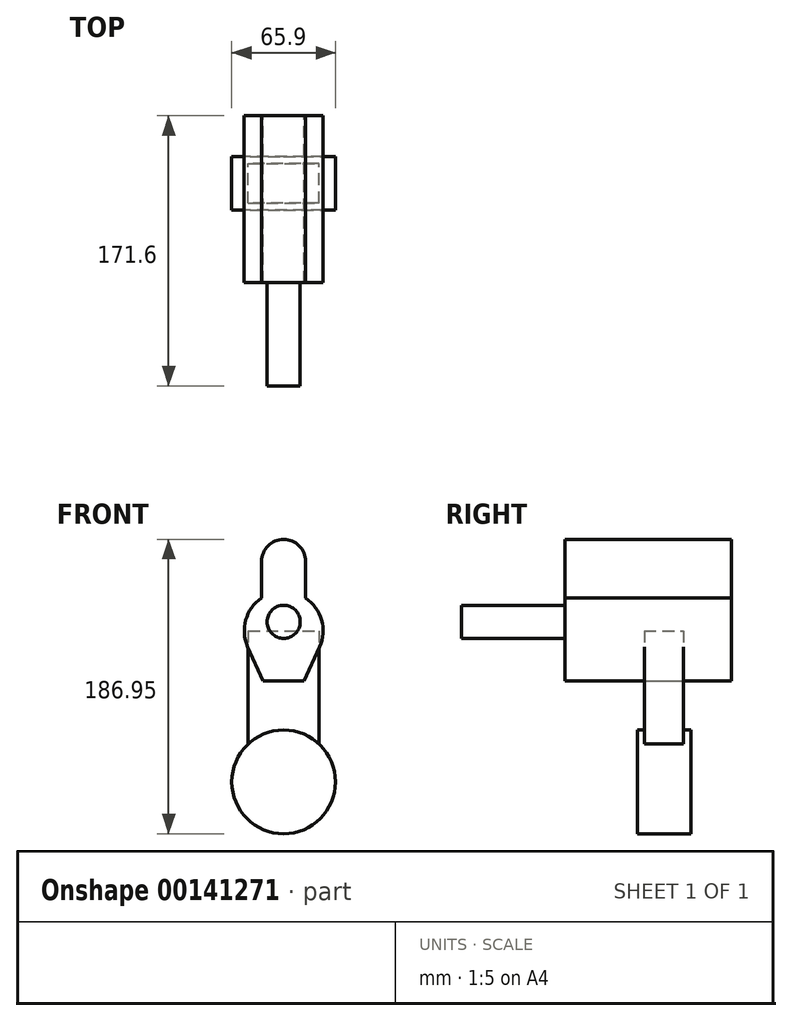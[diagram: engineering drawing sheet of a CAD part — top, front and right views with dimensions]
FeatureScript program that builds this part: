
annotation { "Feature Type Name" : "Feature", "Feature Type Description" : "" }
export const myFeature = defineFeature(function(context is Context, id is Id, definition is map)
    precondition{}
    {
        {
            var Q0;
            Q0=qCreatedBy(makeId("Front.planeOp"),FACE);
            var sketch = newSketch(context, id + "F0", { "sketchPlane" : qUnion([Q0])});
            skCircle(sketch, "E0", {"center": v(0, 0) * mm, "radius": 32.95 * mm});
            skCircle(sketch, "E1", {"center": v(0, 0) * mm, "radius": 20.6 * mm});
            skLineSegment(sketch, "E2.bottom", {"start": v(-22.5, 96) * mm, "end": v(22.5, 96) * mm});
            skLineSegment(sketch, "E2.left", {"start": v(-22.5, 96) * mm, "end": v(-22.5, 24.07) * mm});
            skLineSegment(sketch, "E2.right", {"start": v(22.5, 96) * mm, "end": v(22.5, 24.07) * mm});
            skArc(sketch, "E3", {"start": v(22.8, 85.73) * mm, "mid": v(24.05, 102.82) * mm, "end": v(14, 116.71) * mm});
            skLineSegment(sketch, "E4", {"start": v(-13, 64) * mm, "end": v(13, 64) * mm});
            skLineSegment(sketch, "E5", {"start": v(13, 64) * mm, "end": v(22.8, 85.73) * mm});
            skLineSegment(sketch, "E6", {"start": v(-13, 64) * mm, "end": v(-22.8, 85.73) * mm});
            skLineSegment(sketch, "E7", {"start": v(-14, 116.71) * mm, "end": v(-14, 140) * mm});
            skLineSegment(sketch, "E8", {"start": v(14, 116.71) * mm, "end": v(14, 140) * mm});
            skArc(sketch, "E9", {"start": v(14, 140) * mm, "mid": v(0, 154) * mm, "end": v(-14, 140) * mm});
            skArc(sketch, "E10.trimOffspring", {"start": v(-14, 116.71) * mm, "mid": v(-24.05, 102.82) * mm, "end": v(-22.8, 85.73) * mm});
            skSolve(sketch);
        }
        {
            var Q0;
            {var subQ5=sQuery(id+"F0.wireOp",EDGE,"E2.left");var subQ8=sQuery(id+"F0.wireOp",EDGE,"E0");var subQ9=makeQuery(id+"F0.imprint","INTERSECT",VERTEX,{"derivedFrom":[subQ8,subQ5]});Q0=makeQuery(id+"F0.imprint","IMPRINT",FACE,{"disambiguationData":[TD([[makeQuery(id+"F0.imprint","IMPRINT",EDGE,{"disambiguationData":[TD([[subQ9,-1.0]])],"derivedFrom":subQ8}),1.0]])]});}
            var Q1;
            {var subQ0=sQuery(id+"F0.wireOp",EDGE,"E2.top");var subQ1=sQuery(id+"F0.wireOp",EDGE,"E1");var subQ2=makeQuery(id+"F0.imprint","INTERSECT",VERTEX,{"disambiguationData":[OD(0.0)],"derivedFrom":[subQ1,subQ0]});Q1=makeQuery(id+"F0.imprint","IMPRINT",FACE,{"disambiguationData":[TD([[makeQuery(id+"F0.imprint","IMPRINT",EDGE,{"disambiguationData":[TD([[subQ2,1.0]])],"derivedFrom":subQ1}),1.0]])]});}
            var Q2;
            {var subQ0=sQuery(id+"F0.wireOp",EDGE,"E2.top");var subQ1=sQuery(id+"F0.wireOp",EDGE,"E1");var subQ2=makeQuery(id+"F0.imprint","INTERSECT",VERTEX,{"disambiguationData":[OD(0.0)],"derivedFrom":[subQ1,subQ0]});Q2=makeQuery(id+"F0.imprint","IMPRINT",FACE,{"disambiguationData":[TD([[makeQuery(id+"F0.imprint","IMPRINT",EDGE,{"disambiguationData":[TD([[subQ2,-1.0]])],"derivedFrom":subQ1}),1.0]])]});}
            var Q3;
            {var subQ5=sQuery(id+"F0.wireOp",EDGE,"E2.left");var subQ8=sQuery(id+"F0.wireOp",EDGE,"E0");var subQ9=makeQuery(id+"F0.imprint","INTERSECT",VERTEX,{"derivedFrom":[subQ8,subQ5]});Q3=makeQuery(id+"F0.imprint","IMPRINT",FACE,{"disambiguationData":[TD([[makeQuery(id+"F0.imprint","IMPRINT",EDGE,{"disambiguationData":[TD([[subQ9,1.0]])],"derivedFrom":subQ8}),1.0]])]});}
            extrude(context, id + "F1", {"entities" : qUnion([Q0, Q1, Q2, Q3]), "endBound" : BoundingType.SYMMETRIC, "depth" : 34 * mm});
        }
        {
            var Q0;
            {var subQ0=sQuery(id+"F0.wireOp",EDGE,"E4");Q0=makeQuery(id+"F0.imprint","IMPRINT",FACE,{"disambiguationData":[TD([[makeQuery(id+"F0.imprint","IMPRINT",EDGE,{"derivedFrom":subQ0}),-1.0]])]});}
            var Q1;
            {var subQ2=sQuery(id+"F0.wireOp",EDGE,"E2.bottom");Q1=makeQuery(id+"F0.imprint","IMPRINT",FACE,{"disambiguationData":[TD([[makeQuery(id+"F0.imprint","IMPRINT",EDGE,{"derivedFrom":subQ2}),-1.0]])]});}
            extrude(context, id + "F2", {"entities" : qUnion([Q0, Q1]), "operationType" : NewBodyOperationType.ADD, "endBound" : BoundingType.SYMMETRIC, "depth" : 25 * mm});
        }
        {
            var Q0;
            Q0=qCreatedBy(makeId("Front.planeOp"),FACE);
            var sketch = newSketch(context, id + "F3", { "sketchPlane" : qUnion([Q0])});
            skLineSegment(sketch, "E11.0.2", {"start": v(22.5, 96) * mm, "end": v(22.5, 85.08) * mm});
            skLineSegment(sketch, "E11.0.3", {"start": v(22.5, 85.08) * mm, "end": v(22.8, 85.73) * mm});
            skArc(sketch, "E11.0.4", {"start": v(22.8, 85.73) * mm, "mid": v(24.05, 102.82) * mm, "end": v(14, 116.71) * mm});
            skLineSegment(sketch, "E11.0.5", {"start": v(14, 116.71) * mm, "end": v(14, 140) * mm});
            skArc(sketch, "E11.0.6", {"start": v(14, 140) * mm, "mid": v(0, 154) * mm, "end": v(-14, 140) * mm});
            skLineSegment(sketch, "E11.0.7", {"start": v(-14, 140) * mm, "end": v(-14, 116.71) * mm});
            skArc(sketch, "E11.0.8", {"start": v(-14, 116.71) * mm, "mid": v(-24.05, 102.82) * mm, "end": v(-22.8, 85.73) * mm});
            skLineSegment(sketch, "E11.0.9", {"start": v(-22.8, 85.73) * mm, "end": v(-22.5, 85.08) * mm});
            skLineSegment(sketch, "E12.0", {"start": v(13, 64) * mm, "end": v(22.8, 85.73) * mm});
            skLineSegment(sketch, "E12.1", {"start": v(-13, 64) * mm, "end": v(13, 64) * mm});
            skLineSegment(sketch, "E12.2", {"start": v(-13, 64) * mm, "end": v(-22.8, 85.73) * mm});
            skSolve(sketch);
        }
        {
            var Q0;
            Q0 = qSketchRegion(id + "F3", true);
            extrude(context, id + "F4", {"entities" : qUnion([Q0]), "endBound" : BoundingType.SYMMETRIC, "offsetDistance" : 25 * mm, "depth" : 86 * mm});
        }
        {
            var Q0;
            Q0=makeQuery(id+"F4.opExtrude","CAP_FACE",FACE,{"disambiguationData":[OSD([sQuery(id+"F3.wireOp",EDGE,"E11.0.4"),sQuery(id+"F3.wireOp",EDGE,"E11.0.5"),sQuery(id+"F3.wireOp",EDGE,"E11.0.6"),sQuery(id+"F3.wireOp",EDGE,"E11.0.7"),sQuery(id+"F3.wireOp",EDGE,"E11.0.8"),sQuery(id+"F3.wireOp",EDGE,"E12.0"),sQuery(id+"F3.wireOp",EDGE,"E12.1"),sQuery(id+"F3.wireOp",EDGE,"E12.2")])],"isStart":false});
            extrude(context, id + "F5", {"entities" : qUnion([Q0]), "operationType" : NewBodyOperationType.ADD, "offsetDistance" : 25 * mm, "depth" : 20 * mm});
        }
        {
            var Q0;
            Q0=makeQuery(id+"F5.opExtrude","CAP_FACE",FACE,{"disambiguationData":[OSD([sQuery(id+"F3.wireOp",EDGE,"E11.0.4"),sQuery(id+"F3.wireOp",EDGE,"E11.0.5"),sQuery(id+"F3.wireOp",EDGE,"E11.0.6"),sQuery(id+"F3.wireOp",EDGE,"E11.0.7"),sQuery(id+"F3.wireOp",EDGE,"E11.0.8"),sQuery(id+"F3.wireOp",EDGE,"E12.0"),sQuery(id+"F3.wireOp",EDGE,"E12.1"),sQuery(id+"F3.wireOp",EDGE,"E12.2")])],"isStart":false});
            var sketch = newSketch(context, id + "F6", { "sketchPlane" : qUnion([Q0])});
            skCircle(sketch, "E13", {"center": v(0, 101.6) * mm, "radius": 10.52 * mm});
            skSolve(sketch);
        }
        {
            var Q0;
            Q0 = qSketchRegion(id + "F6", true);
            extrude(context, id + "F7", {"entities" : qUnion([Q0]), "operationType" : NewBodyOperationType.ADD, "depth" : 65.6 * mm, "offsetDistance" : 25 * mm});
        }
    });
